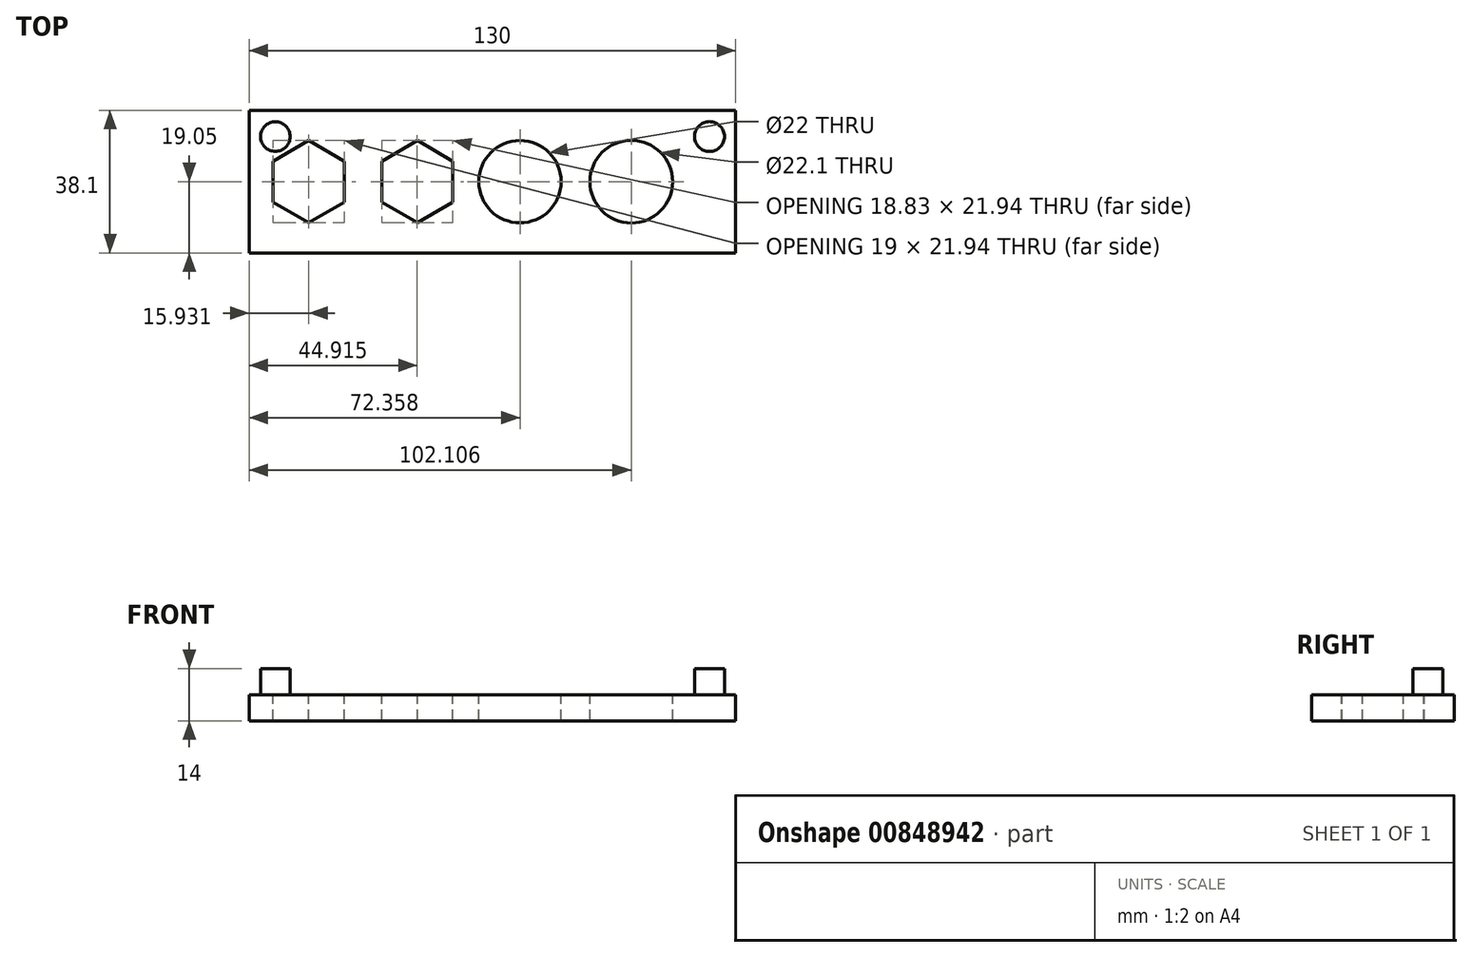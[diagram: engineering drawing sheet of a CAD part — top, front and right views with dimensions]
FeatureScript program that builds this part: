
annotation { "Feature Type Name" : "Feature", "Feature Type Description" : "" }
export const myFeature = defineFeature(function(context is Context, id is Id, definition is map)
    precondition{}
    {
        {
            var Q0;
            Q0=qCreatedBy(makeId("Top.planeOp"),FACE);
            var sketch = newSketch(context, id + "F0", { "sketchPlane" : qUnion([Q0])});
            skLineSegment(sketch, "E0.bottom", {"start": v(85, 19.05) * mm, "end": v(-45, 19.05) * mm});
            skLineSegment(sketch, "E0.top", {"start": v(85, -19.05) * mm, "end": v(-45, -19.05) * mm});
            skLineSegment(sketch, "E0.left", {"start": v(85, 19.05) * mm, "end": v(85, -19.05) * mm});
            skLineSegment(sketch, "E0.right", {"start": v(-45, 19.05) * mm, "end": v(-45, -19.05) * mm});
            skSolve(sketch);
        }
        {
            var Q0;
            Q0=makeQuery(id+"F0.imprint","IMPRINT",FACE,{"disambiguationData":[TD([[makeQuery(id+"F0.imprint","IMPRINT",EDGE,{"derivedFrom":sQuery(id+"F0.wireOp",EDGE,"E0.bottom")}),1.0]])]});
            var sketch = newSketch(context, id + "F1", { "sketchPlane" : qUnion([Q0])});
            skLineSegment(sketch, "E1.0", {"start": v(9.33, 5.48) * mm, "end": v(9.33, -5.48) * mm});
            skLineSegment(sketch, "E1.1", {"start": v(9.33, -5.48) * mm, "end": v(0, -10.97) * mm});
            skLineSegment(sketch, "E1.2", {"start": v(0, -10.97) * mm, "end": v(-9.5, -5.48) * mm});
            skLineSegment(sketch, "E1.3", {"start": v(-9.5, -5.48) * mm, "end": v(-9.5, 5.48) * mm});
            skLineSegment(sketch, "E1.4", {"start": v(-9.5, 5.48) * mm, "end": v(0, 10.97) * mm});
            skLineSegment(sketch, "E1.5", {"start": v(0, 10.97) * mm, "end": v(9.33, 5.48) * mm});
            skPoint(sketch, "E1.0.midPoint", {"position": v(9.33, 0) * mm});
            skCircle(sketch, "E2", {"center": v(27.36, 0) * mm, "radius": 11 * mm});
            skCircle(sketch, "E3.cCircle", {"center": v(-29.07, 0) * mm, "radius": 9.5 * mm, "construction": true});
            skLineSegment(sketch, "E3.0", {"start": v(-19.57, 5.48) * mm, "end": v(-19.57, -5.48) * mm});
            skLineSegment(sketch, "E3.1", {"start": v(-19.57, -5.48) * mm, "end": v(-29.07, -10.97) * mm});
            skLineSegment(sketch, "E3.2", {"start": v(-29.07, -10.97) * mm, "end": v(-38.57, -5.48) * mm});
            skLineSegment(sketch, "E3.3", {"start": v(-38.57, -5.48) * mm, "end": v(-38.57, 5.48) * mm});
            skLineSegment(sketch, "E3.4", {"start": v(-38.57, 5.48) * mm, "end": v(-29.07, 10.97) * mm});
            skLineSegment(sketch, "E3.5", {"start": v(-29.07, 10.97) * mm, "end": v(-19.57, 5.48) * mm});
            skPoint(sketch, "E3.0.midPoint", {"position": v(-19.57, 0) * mm});
            skCircle(sketch, "E4", {"center": v(57.1, 0) * mm, "radius": 11.05 * mm});
            skSolve(sketch);
        }
        {
            var Q0;
            Q0 = qSketchRegion(id + "F0", true);
            extrude(context, id + "F2", {"entities" : qUnion([Q0]), "depth" : 7 * mm, "offsetDistance" : 25.4 * mm, "symmetric" : true});
        }
        {
            var Q0;
            Q0 = qSketchRegion(id + "F1", true);
            extrude(context, id + "F3", {"entities" : qUnion([Q0]), "operationType" : NewBodyOperationType.REMOVE, "oppositeDirection" : true, "depth" : 25 * mm, "offsetDistance" : 25 * mm, "symmetric" : true});
        }
        {
            var Q0;
            Q0=makeQuery(id+"F2.opExtrude","CAP_FACE",FACE,{"disambiguationData":[OSD([sQuery(id+"F0.wireOp",EDGE,"E0.bottom"),sQuery(id+"F0.wireOp",EDGE,"E0.top"),sQuery(id+"F0.wireOp",EDGE,"E0.left"),sQuery(id+"F0.wireOp",EDGE,"E0.right")])],"isStart":false});
            var sketch = newSketch(context, id + "F4", { "sketchPlane" : qUnion([Q0])});
            skCircle(sketch, "E5", {"center": v(78, 12.05) * mm, "radius": 4 * mm});
            skCircle(sketch, "E6", {"center": v(-38, 12.05) * mm, "radius": 3.95 * mm});
            skSolve(sketch);
        }
        {
            var Q0;
            Q0 = qSketchRegion(id + "F4", true);
            extrude(context, id + "F5", {"entities" : qUnion([Q0]), "operationType" : NewBodyOperationType.ADD, "depth" : 7 * mm, "offsetDistance" : 25 * mm});
        }
    });
